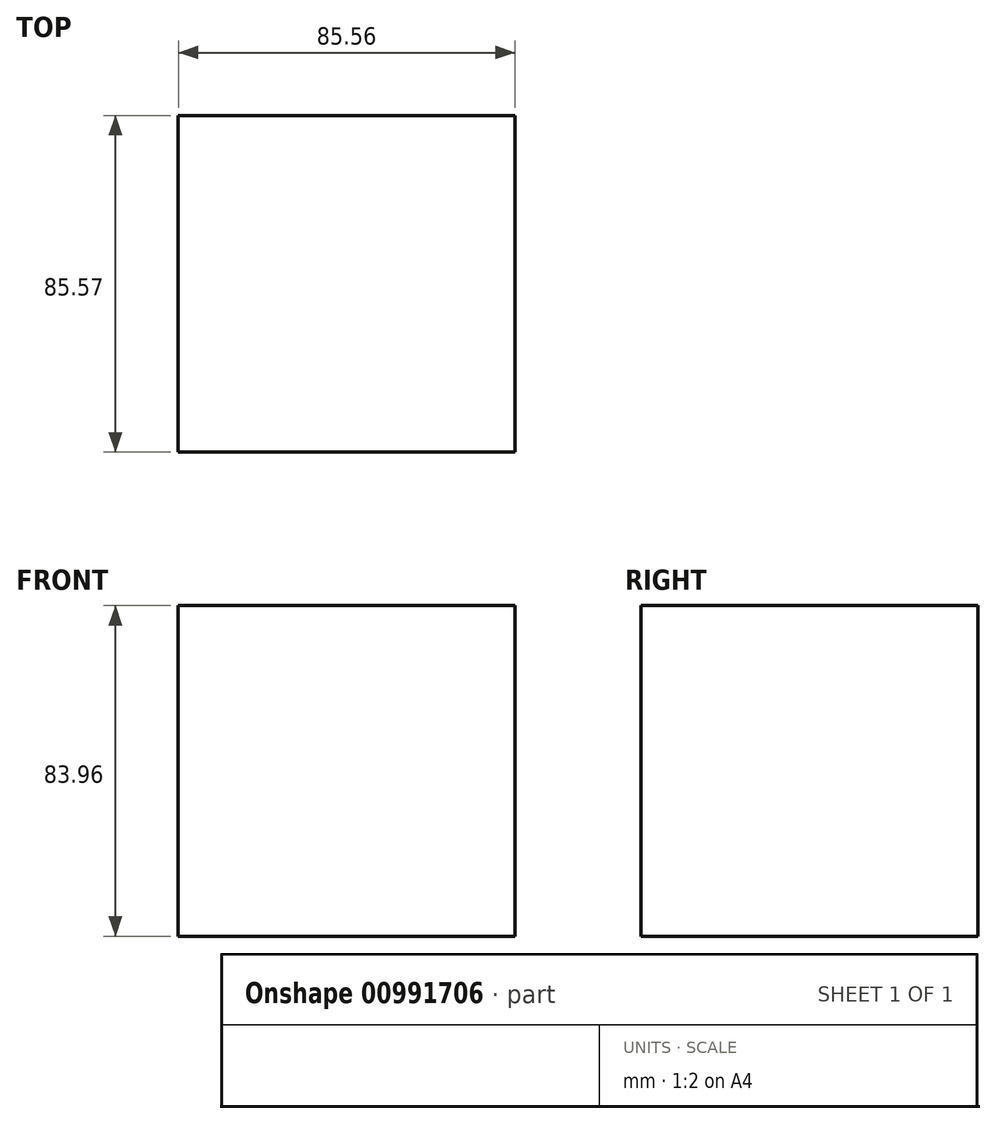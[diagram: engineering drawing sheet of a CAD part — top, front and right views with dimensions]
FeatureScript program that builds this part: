
annotation { "Feature Type Name" : "Feature", "Feature Type Description" : "" }
export const myFeature = defineFeature(function(context is Context, id is Id, definition is map)
    precondition{}
    {
        {
            var Q0;
            Q0=qCreatedBy(makeId("Top.planeOp"),FACE);
            var sketch = newSketch(context, id + "F0", { "sketchPlane" : qUnion([Q0])});
            skLineSegment(sketch, "E0", {"start": v(44.2, 33.27) * mm, "end": v(-41.36, 33.27) * mm});
            skLineSegment(sketch, "E1", {"start": v(-41.36, 33.27) * mm, "end": v(-41.36, -52.3) * mm});
            skLineSegment(sketch, "E2", {"start": v(-41.36, -52.3) * mm, "end": v(44.2, -52.3) * mm});
            skLineSegment(sketch, "E3", {"start": v(44.2, -52.3) * mm, "end": v(44.2, 33.27) * mm});
            skSolve(sketch);
        }
        {
            var Q0;
            Q0 = qSketchRegion(id + "F0", true);
            var Q1;
            Q1=makeQuery(id+"F0.imprint","IMPRINT",FACE,{"disambiguationData":[TD([[makeQuery(id+"F0.imprint","IMPRINT",EDGE,{"derivedFrom":sQuery(id+"F0.wireOp",EDGE,"E0")}),1.0]])]});
            extrude(context, id + "F1", {"entities" : qUnion([Q0, Q1]), "depth" : 83.96 * mm, "offsetDistance" : 25 * mm});
        }
    });
